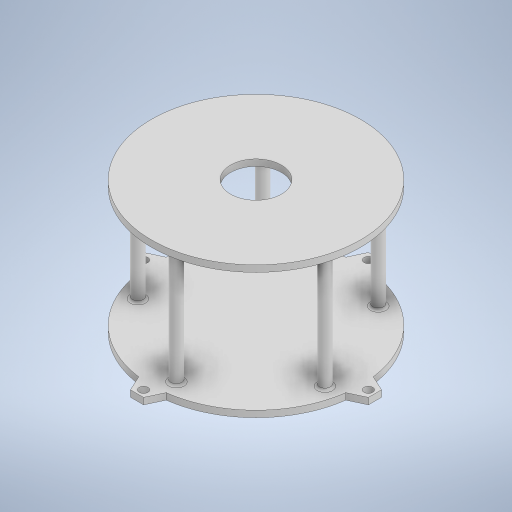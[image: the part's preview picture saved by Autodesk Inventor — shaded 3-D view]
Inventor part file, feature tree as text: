
AUTODESK INVENTOR PART (.ipt)
format: ipt  version: 2023 (Build 270158000, 158)  size: 348,672 bytes
history: native  units: mm
features: extrude x6, sketch x6, pattern_circular x2, other x1, plane x1, fillet x1
ambient origin geometry x8: Origin, YZ Plane, XZ Plane, XY Plane, X Axis, Y Axis, Z Axis, Center Point
bodies: Body1 (feature_tree)
feature tree (17):
  other  "Sólido1"
  extrude  "Extrusión1"  Depth=2.96mm TaperAngle=0.0deg
  plane  "Plano de trabajo1"
  extrude  "Extrusión2"  Depth=2.96mm TaperAngle=0.0deg
  extrude  "Extrusión3"  Depth=4.0mm
  pattern_circular  "Patrón circular1"  [2 undecoded]
  extrude  "Extrusión4"  Depth=2.96mm TaperAngle=0.0deg
  fillet  "Empalme1"  Radius=40.0mm
  pattern_circular  "Patrón circular2"  [2 undecoded]
  extrude  "Extrusión5"  TaperAngle=30.0deg  [1 undecoded]
  extrude  "Extrusión6"  Depth=5.0mm
  sketch  "Boceto1"  dims[d0=95.7mm d1=2.96mm d2=0.0mm]
  sketch  "Boceto2"  dims[d3=54.7mm d4=2.96mm d5=0.0mm]
  sketch  "Boceto3"  dims[d6=103.0mm d7=4.0mm]
  sketch  "Boceto4"  dims[d8=20.071286mm]
  sketch  "Boceto5"  dims[d9=20.071286mm]
  sketch  "Boceto6"  dims[d10=3.0mm d11=6.0mm d12=2.96mm d13=0.0mm d14=40.0mm d15=360.0deg d17=82.0mm d18=30.0deg d19=5.0mm d20=2.96mm d21=0.0mm d22=1.0mm d23=50.0mm d24=360.0deg d26=23.2mm d27=10.0mm d28=0.0mm d29=0.5mm d30=0.0mm d25=0.0mm]
note: 5 required parameter values undecoded (feature->parameter linkage not recoverable at this tier; creation-order binding heuristic only, values carry confidence <= 0.55)
